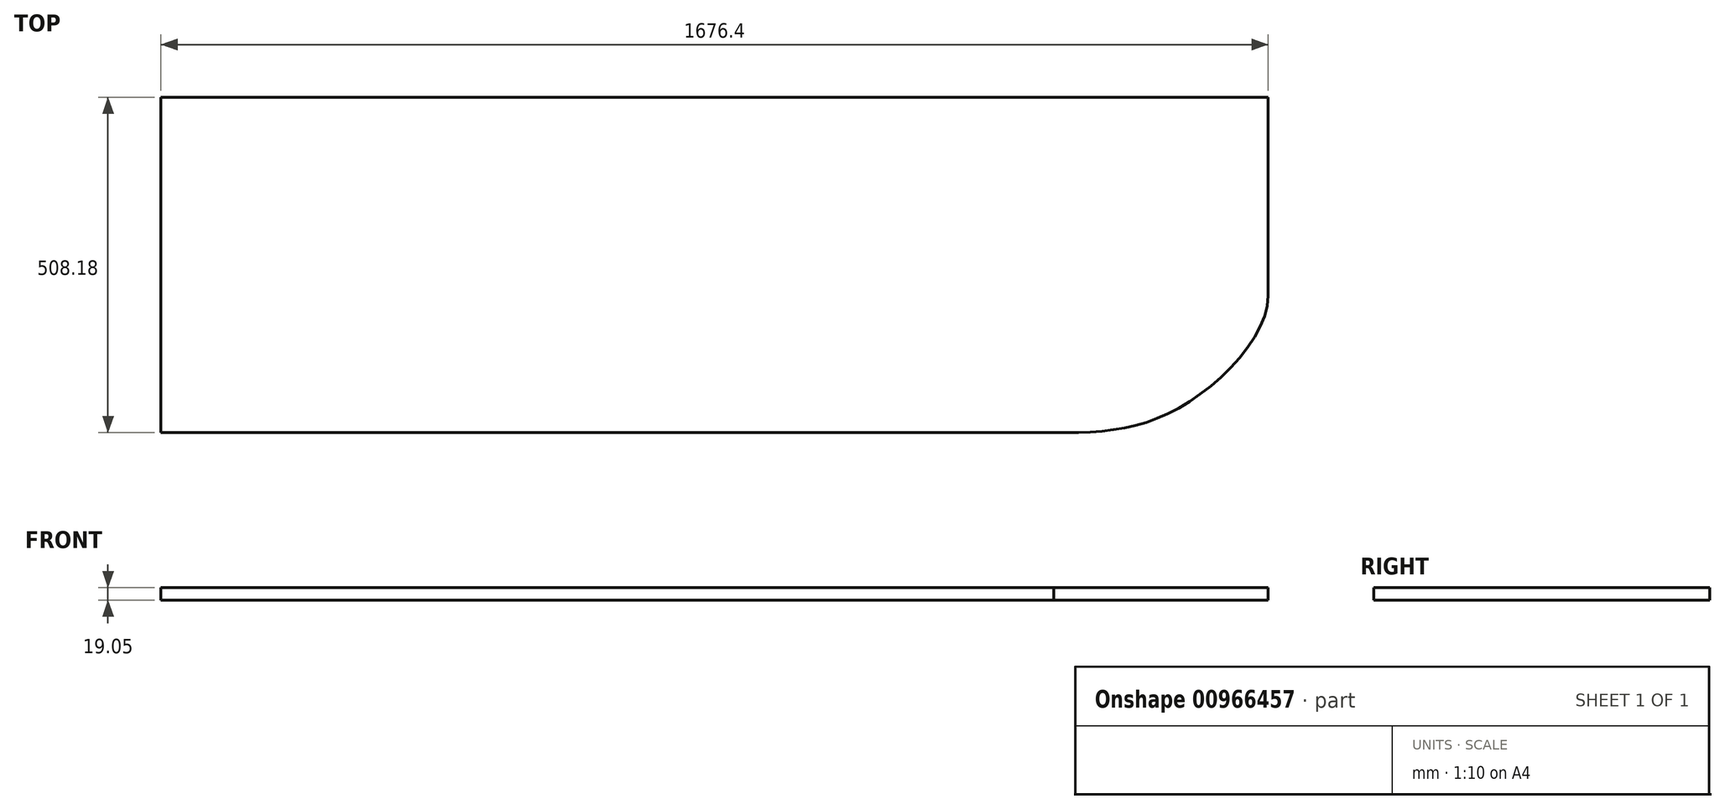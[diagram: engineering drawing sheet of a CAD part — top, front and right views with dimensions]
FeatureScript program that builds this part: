
annotation { "Feature Type Name" : "Feature", "Feature Type Description" : "" }
export const myFeature = defineFeature(function(context is Context, id is Id, definition is map)
    precondition{}
    {
        {
            var Q0;
            Q0=qCreatedBy(makeId("Top.planeOp"),FACE);
            var sketch = newSketch(context, id + "F0", { "sketchPlane" : qUnion([Q0])});
            skLineSegment(sketch, "E0.bottom", {"start": v(0, 0) * mm, "end": v(1676.4, 0) * mm});
            skLineSegment(sketch, "E0.top", {"start": v(0, -508) * mm, "end": v(1351.8, -508) * mm});
            skLineSegment(sketch, "E0.left", {"start": v(0, 0) * mm, "end": v(0, -508) * mm});
            skLineSegment(sketch, "E0.right", {"start": v(1676.4, 0) * mm, "end": v(1676.4, -300.8) * mm});
            skLineSegment(sketch, "E1", {"start": v(1351.8, -508) * mm, "end": v(1351.8, -508) * mm});
            skFitSpline(sketch, "E2", {"points": [v(1351.8, -508) * mm, v(1545.64, -468.47) * mm, v(1676.4, -300.8) * mm], "startDerivative": vector(444.48, -7.68) * mm, "endDerivative": vector(0, 346.95) * mm});
            skPoint(sketch, "E3", {"position": v(1676.4, -404.4) * mm});
            skPoint(sketch, "E4.orphan", {"position": v(1676.4, -508) * mm});
            skSolve(sketch);
        }
        {
            var Q0;
            Q0 = qSketchRegion(id + "F0", true);
            extrude(context, id + "F1", {"entities" : qUnion([Q0]), "depth" : 19.05 * mm, "offsetDistance" : 25.4 * mm});
        }
    });
